FCSTD DOCUMENT  (FreeCAD 0.16R6712 (Git))
Label: bras_moteur
License: All rights reserved
LicenseURL: http://en.wikipedia.org/wiki/All_rights_reserved
objects: Sketcher::SketchObject×5, PartDesign::Pad×3, Mesh::Feature×2, PartDesign::Pocket×2
note: 15 computed .brp shape members not serialized (recipe doc carries the construction recipe); baked Part::Feature solids carry a one-line shape summary decoded from their .brp

FEATURE [Sketcher::SketchObject] Sketch
  sketch-geometry (4):
    g0: LineSegment StartX=-15 StartY=15 StartZ=0 EndX=15 EndY=15 EndZ=0
    g1: LineSegment StartX=15 StartY=15 StartZ=0 EndX=15 EndY=-15 EndZ=0
    g2: LineSegment StartX=15 StartY=-15 StartZ=0 EndX=-15 EndY=-15 EndZ=0
    g3: LineSegment StartX=-15 StartY=-15 StartZ=0 EndX=-15 EndY=15 EndZ=0
  constraints (12):
    c: Coincident(g0,g1)
    c: Coincident(g1,g2)
    c: Coincident(g2,g3)
    c: Coincident(g3,g0)
    c: Horizontal(g0)
    c: Horizontal(g2)
    c: Vertical(g1)
    c: Vertical(g3)
    c: Distance(g1) = 30
    c: Distance(g2) = 30
    c: Symmetric(g2,g1,g-2)
    c: Symmetric(g0,g1,g-1)
FEATURE [PartDesign::Pad] Pad
  Length = 3
  Length2 = 100
  Sketch = -> Sketch
  Type = 0
FEATURE [Sketcher::SketchObject] Sketch001
  ExternalGeometry = -> [Pad]
  Placement = pos=(0,0,3) rot=(0,0,1;0rad)
  Support = -> Pad [Face6]
  sketch-geometry (4):
    g0: LineSegment StartX=15 StartY=3 StartZ=0 EndX=-70 EndY=3 EndZ=0
    g1: LineSegment StartX=-70 StartY=3 StartZ=0 EndX=-70 EndY=-3 EndZ=0
    g2: LineSegment StartX=-70 StartY=-3 StartZ=0 EndX=15 EndY=-3 EndZ=0
    g3: LineSegment StartX=15 StartY=-3 StartZ=0 EndX=15 EndY=3 EndZ=0
  constraints (12):
    c: Coincident(g0,g1)
    c: Coincident(g1,g2)
    c: Coincident(g2,g3)
    c: Coincident(g3,g0)
    c: Horizontal(g0)
    c: Horizontal(g2)
    c: Vertical(g1)
    c: Vertical(g3)
    c: Symmetric(g2,g0,g-1)
    c: DistanceY(g3,g3) = 6
    c: DistanceX(g0,g-4) = 55
    c: PointOnObject(g0,g-3)
FEATURE [PartDesign::Pad] Pad001
  Length = 6
  Length2 = 100
  Reversed = true
  Sketch = -> Sketch001
  Type = 0
FEATURE [Sketcher::SketchObject] Sketch002
  ExternalGeometry = -> [Pad001]
  Placement = pos=(-70,0,0) rot=(0.57735,-0.57735,-0.57735;2.0944rad)
  Support = -> Pad001 [Face10]
  sketch-geometry (1):
    g0: Circle CenterX=0 CenterY=0 CenterZ=0 NormalX=0 NormalY=0 NormalZ=1 Radius=2.3
  constraints (3):
    c: PointOnObject(g0,g-2)
    c: Radius(g0) = 2.3
    c: Coincident(g0,g-1)
FEATURE [PartDesign::Pad] Pad002
  Length = 20
  Length2 = 100
  Sketch = -> Sketch002
  Type = 0
FEATURE [Mesh::Feature] Moteur
  Placement = pos=(13,-17.5,3) rot=(0,0,-1;0.191986rad)
FEATURE [Sketcher::SketchObject] Sketch003
  ExternalGeometry = -> [Pad002]
  Placement = pos=(0,3,0) rot=(0,0.707107,0.707107;3.14159rad)
  Support = -> Pad002 [Face6]
  sketch-geometry (1):
    g0: Circle CenterX=67 CenterY=0 CenterZ=0 NormalX=0 NormalY=0 NormalZ=1 Radius=1.5
  constraints (3):
    c: PointOnObject(g0,g-1)
    c: Radius(g0) = 1.5
    c: DistanceX(g0,g-3) = 3
FEATURE [PartDesign::Pocket] Pocket
  Length = 5
  Sketch = -> Sketch003
  Type = 1
FEATURE [Sketcher::SketchObject] Sketch004
  Placement = pos=(0,0,3) rot=(0,0,1;0rad)
  Support = -> Pocket [Face15]
  sketch-geometry (10):
    g0: Circle CenterX=-5.65685 CenterY=5.65685 CenterZ=0 NormalX=0 NormalY=0 NormalZ=1 Radius=1.75
    g1: Circle CenterX=6.71751 CenterY=6.71751 CenterZ=0 NormalX=0 NormalY=0 NormalZ=1 Radius=1.75
    g2: Circle CenterX=-6.71751 CenterY=-6.71751 CenterZ=0 NormalX=0 NormalY=0 NormalZ=1 Radius=1.75
    g3: Circle CenterX=5.65685 CenterY=-5.65685 CenterZ=0 NormalX=0 NormalY=0 NormalZ=1 Radius=1.75
    g4: LineSegment [constr] StartX=-6.71751 StartY=-6.71751 StartZ=0 EndX=6.71751 EndY=6.71751 EndZ=0
    g5: LineSegment [constr] StartX=-5.65685 StartY=5.65685 StartZ=0 EndX=5.65685 EndY=-5.65685 EndZ=0
    g6: LineSegment StartX=-3.75 StartY=3.75 StartZ=0 EndX=3.75 EndY=3.75 EndZ=0
    g7: LineSegment StartX=3.75 StartY=3.75 StartZ=0 EndX=3.75 EndY=-3.75 EndZ=0
    g8: LineSegment StartX=3.75 StartY=-3.75 StartZ=0 EndX=-3.75 EndY=-3.75 EndZ=0
    g9: LineSegment StartX=-3.75 StartY=-3.75 StartZ=0 EndX=-3.75 EndY=3.75 EndZ=0
  constraints (27):
    c: PointOnObject(g-1,g5)
    c: PointOnObject(g-1,g4)
    c: Coincident(g0,g5)
    c: Coincident(g1,g4)
    c: Coincident(g2,g4)
    c: Coincident(g3,g5)
    c: Angle(g5,g-1) = 0.785398
    c: Radius(g3) = 1.75
    c: Equal(g3,g2)
    c: Equal(g3,g0)
    c: Equal(g3,g1)
    c: Distance(g4) = 19
    c: Distance(g5) = 16
    c: Symmetric(g1,g2,g5)
    c: Symmetric(g3,g0,g4)
    c: Coincident(g6,g7)
    c: Coincident(g7,g8)
    c: Coincident(g8,g9)
    c: Coincident(g9,g6)
    c: Horizontal(g6)
    c: Horizontal(g8)
    c: Vertical(g7)
    c: Vertical(g9)
    c: PointOnObject(g7,g5)
    c: Symmetric(g8,g6,g-1)
    c: Symmetric(g7,g8,g-2)
    c: DistanceX(g8,g8) = 7.5
FEATURE [PartDesign::Pocket] Pocket001
  Length = 5
  Sketch = -> Sketch004
  Type = 1
FEATURE [Mesh::Feature] Helice
  Placement = pos=(0,0,19.7) rot=(0,0,1;0rad)
